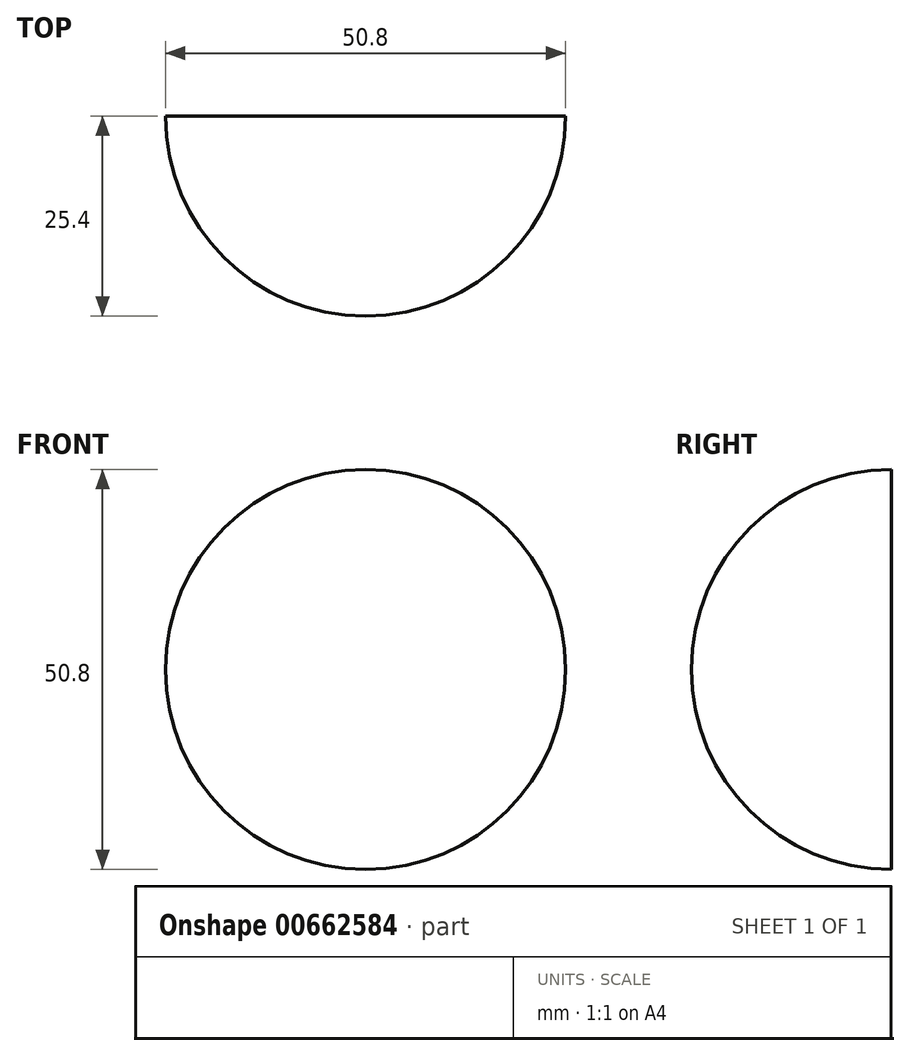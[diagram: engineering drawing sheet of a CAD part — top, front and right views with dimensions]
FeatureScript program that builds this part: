
annotation { "Feature Type Name" : "Feature", "Feature Type Description" : "" }
export const myFeature = defineFeature(function(context is Context, id is Id, definition is map)
    precondition{}
    {
        {
            var Q0;
            Q0=qCreatedBy(makeId("Front.planeOp"),FACE);
            var sketch = newSketch(context, id + "F0", { "sketchPlane" : qUnion([Q0])});
            skLineSegment(sketch, "E0", {"start": v(0, 0) * mm, "end": v(0, 50.8) * mm});
            skArc(sketch, "E1", {"start": v(0, 0) * mm, "mid": v(25.4, 25.4) * mm, "end": v(0, 50.8) * mm});
            skSolve(sketch);
        }
        {
            var Q0;
            Q0=makeQuery(id+"F0.imprint","IMPRINT",FACE,{"disambiguationData":[TD([[makeQuery(id+"F0.imprint","IMPRINT",EDGE,{"derivedFrom":sQuery(id+"F0.wireOp",EDGE,"E0")}),-1.0]])]});
            var Q1;
            Q1=sQuery(id+"F0.wireOp",EDGE,"E0");
            revolve(context, id + "F1", {"entities" : qUnion([Q0]), "axis" : qUnion([Q1]), "revolveType" : RevolveType.TWO_DIRECTIONS, "oppositeDirection" : true, "angle" : 180 * degree, "angleBack" : 360 * degree});
        }
    });
